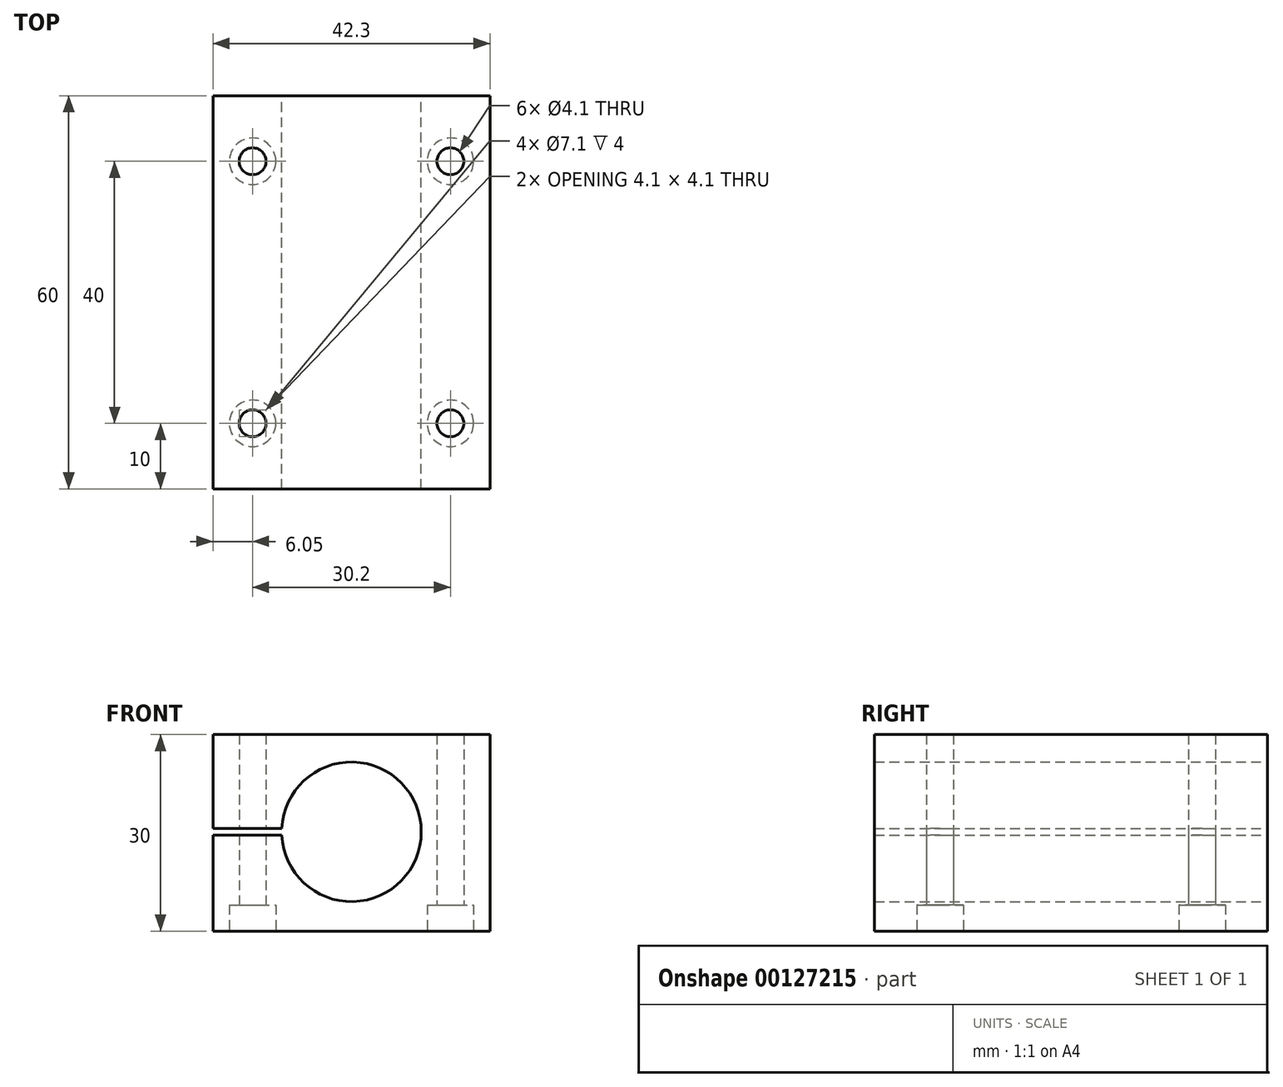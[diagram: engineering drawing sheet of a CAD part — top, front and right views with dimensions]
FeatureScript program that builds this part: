
annotation { "Feature Type Name" : "Feature", "Feature Type Description" : "" }
export const myFeature = defineFeature(function(context is Context, id is Id, definition is map)
    precondition{}
    {
        {
            var Q0;
            Q0=qCreatedBy(makeId("Front.planeOp"),FACE);
            var sketch = newSketch(context, id + "F0", { "sketchPlane" : qUnion([Q0])});
            skLineSegment(sketch, "E0", {"start": v(-21.15, 14.85) * mm, "end": v(-21.15, -15.15) * mm});
            skLineSegment(sketch, "E1", {"start": v(-21.15, 14.85) * mm, "end": v(21.15, 14.85) * mm});
            skCircle(sketch, "E2", {"center": v(0, 0) * mm, "radius": 10.65 * mm});
            skLineSegment(sketch, "E3", {"start": v(21.15, 14.85) * mm, "end": v(21.15, -15.15) * mm});
            skLineSegment(sketch, "E4", {"start": v(21.15, -15.15) * mm, "end": v(-21.15, -15.15) * mm});
            skSolve(sketch);
        }
        {
            var Q0;
            Q0=qSketchRegion(id+"F0",true);
            extrude(context, id + "F1", {"entities" : qUnion([Q0]), "depth" : 60 * mm});
        }
        {
            var Q0;
            Q0=makeQuery(id+"F1.opExtrude","SWEPT_FACE",FACE,{"disambiguationData":[OSD([sQuery(id+"F0.wireOp",EDGE,"E4")])]});
            var sketch = newSketch(context, id + "F2", { "sketchPlane" : qUnion([Q0])});
            skLineSegment(sketch, "E5", {"start": v(-21.15, 60) * mm, "end": v(-18.65, 60) * mm});
            skLineSegment(sketch, "E6", {"start": v(-18.65, 60) * mm, "end": v(-11.55, 60) * mm});
            skLineSegment(sketch, "E7", {"start": v(-15.1, 60) * mm, "end": v(-15.1, 50) * mm});
            skLineSegment(sketch, "E8", {"start": v(21.15, 60) * mm, "end": v(18.65, 60) * mm});
            skLineSegment(sketch, "E9", {"start": v(18.65, 60) * mm, "end": v(11.55, 60) * mm});
            skLineSegment(sketch, "E10", {"start": v(15.1, 60) * mm, "end": v(15.1, 50) * mm});
            skLineSegment(sketch, "E11", {"start": v(-21.15, 0) * mm, "end": v(-18.65, 0) * mm});
            skLineSegment(sketch, "E12", {"start": v(-18.65, 0) * mm, "end": v(-11.55, 0) * mm});
            skLineSegment(sketch, "E13", {"start": v(-15.1, 0) * mm, "end": v(-15.1, 10) * mm});
            skLineSegment(sketch, "E14", {"start": v(21.15, 0) * mm, "end": v(18.65, 0) * mm});
            skLineSegment(sketch, "E15", {"start": v(18.65, 0) * mm, "end": v(11.55, 0) * mm});
            skLineSegment(sketch, "E16", {"start": v(15.1, 0) * mm, "end": v(15.1, 10) * mm});
            skCircle(sketch, "E17", {"center": v(-15.1, 50) * mm, "radius": 2.05 * mm});
            skCircle(sketch, "E18", {"center": v(15.1, 50) * mm, "radius": 2.05 * mm});
            skCircle(sketch, "E19", {"center": v(-15.1, 10) * mm, "radius": 2.05 * mm});
            skCircle(sketch, "E20", {"center": v(15.1, 10) * mm, "radius": 2.05 * mm});
            skSolve(sketch);
        }
        {
            var Q0;
            Q0=qSketchRegion(id+"F2",true);
            extrude(context, id + "F3", {"entities" : qUnion([Q0]), "operationType" : NewBodyOperationType.REMOVE, "oppositeDirection" : true, "depth" : 30 * mm});
        }
        {
            var Q0;
            Q0=makeQuery(id+"F1.opExtrude","SWEPT_FACE",FACE,{"disambiguationData":[OSD([sQuery(id+"F0.wireOp",EDGE,"E4")])]});
            var sketch = newSketch(context, id + "F4", { "sketchPlane" : qUnion([Q0])});
            skCircle(sketch, "E21", {"center": v(-15.1, 50) * mm, "radius": 3.55 * mm});
            skCircle(sketch, "E22", {"center": v(15.1, 50) * mm, "radius": 3.55 * mm});
            skCircle(sketch, "E23", {"center": v(-15.1, 10) * mm, "radius": 3.55 * mm});
            skCircle(sketch, "E24", {"center": v(15.1, 10) * mm, "radius": 3.55 * mm});
            skSolve(sketch);
        }
        {
            var Q0;
            Q0=qSketchRegion(id+"F4",true);
            extrude(context, id + "F5", {"entities" : qUnion([Q0]), "operationType" : NewBodyOperationType.REMOVE, "oppositeDirection" : true, "depth" : 4 * mm});
        }
        {
            var Q0;
            Q0=makeQuery(id+"F1.opExtrude","CAP_FACE",FACE,{"disambiguationData":[OSD([sQuery(id+"F0.wireOp",EDGE,"E0"),sQuery(id+"F0.wireOp",EDGE,"E1"),sQuery(id+"F0.wireOp",EDGE,"E2"),sQuery(id+"F0.wireOp",EDGE,"E3"),sQuery(id+"F0.wireOp",EDGE,"E4")])],"isStart":true});
            var sketch = newSketch(context, id + "F6", { "sketchPlane" : qUnion([Q0])});
            skLineSegment(sketch, "E25", {"start": v(21.15, 0) * mm, "end": v(10.65, 0) * mm});
            skLineSegment(sketch, "E26", {"start": v(21.15, 0) * mm, "end": v(21.15, -0.5) * mm});
            skLineSegment(sketch, "E27", {"start": v(21.15, 0) * mm, "end": v(21.15, 0.5) * mm});
            skLineSegment(sketch, "E28", {"start": v(21.15, -0.5) * mm, "end": v(10.64, -0.5) * mm});
            skLineSegment(sketch, "E29", {"start": v(21.15, 0.5) * mm, "end": v(10.64, 0.5) * mm});
            skArc(sketch, "E30", {"start": v(10.64, -0.5) * mm, "mid": v(10.65, 0) * mm, "end": v(10.64, 0.5) * mm});
            skSolve(sketch);
        }
        {
            var Q0;
            Q0=qSketchRegion(id+"F6",true);
            extrude(context, id + "F7", {"entities" : qUnion([Q0]), "operationType" : NewBodyOperationType.REMOVE, "oppositeDirection" : true, "depth" : 60 * mm});
        }
    });
